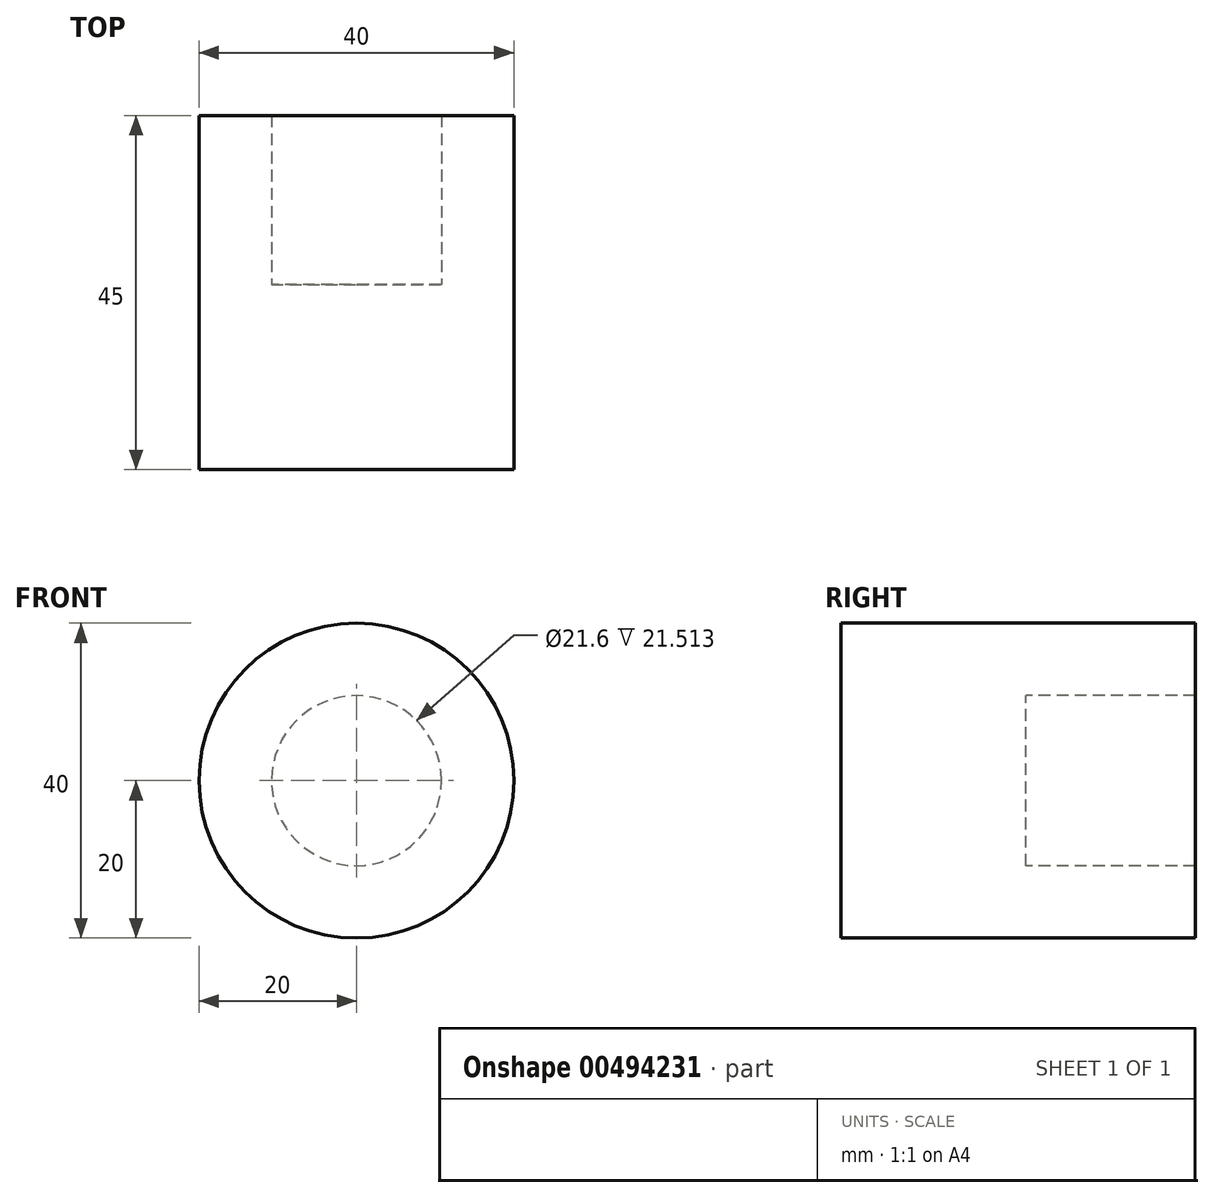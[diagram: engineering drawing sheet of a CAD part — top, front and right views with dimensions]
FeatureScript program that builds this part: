
annotation { "Feature Type Name" : "Feature", "Feature Type Description" : "" }
export const myFeature = defineFeature(function(context is Context, id is Id, definition is map)
    precondition{}
    {
        {
            var Q0;
            Q0=qCreatedBy(makeId("Top.planeOp"),FACE);
            var sketch = newSketch(context, id + "F0", { "sketchPlane" : qUnion([Q0])});
            skLineSegment(sketch, "E0", {"start": v(10.8, 0) * mm, "end": v(10.8, 21.51) * mm});
            skLineSegment(sketch, "E1", {"start": v(10.8, 21.51) * mm, "end": v(20, 21.51) * mm});
            skLineSegment(sketch, "E2", {"start": v(20, 21.51) * mm, "end": v(20, -23.49) * mm});
            skLineSegment(sketch, "E3", {"start": v(20, -23.49) * mm, "end": v(0, -23.49) * mm});
            skLineSegment(sketch, "E4", {"start": v(0, -23.49) * mm, "end": v(0, 0) * mm});
            skLineSegment(sketch, "E5", {"start": v(0, 0) * mm, "end": v(10.8, 0) * mm});
            skSolve(sketch);
        }
        {
            var Q0;
            Q0=makeQuery(id+"F0.imprint","IMPRINT",FACE,{"disambiguationData":[TD([[makeQuery(id+"F0.imprint","IMPRINT",EDGE,{"derivedFrom":sQuery(id+"F0.wireOp",EDGE,"E0")}),-1.0]])]});
            var Q1;
            Q1=sQuery(id+"F0.wireOp",EDGE,"E4");
            revolve(context, id + "F1", {"entities" : qUnion([Q0]), "axis" : qUnion([Q1]), "revolveType" : RevolveType.FULL});
        }
    });
